# Revit family: 210_7b185d169fbb4492bceb13950c4227
name_source: partatom
category: Mechanical Equipment
units: mm (PartAtom-declared; Revit-internal decimal feet)

## family parameters
Always vertical = Yes
Cut with Voids When Loaded = No
Part Type = Breaks Into
Room Calculation Point = No
Round Connector Dimension = Use Diameter
Shared = No
Work Plane-Based = No

## types (1)
- ECo Flow 160S
    A2 = 155 mm  [stored 0.50853 ft]
    BB = 79 mm  [stored 0.259186 ft]
    BB_2 = 40 mm  [stored 0.131234 ft]
    BD = 36 mm  [stored 0.11811 ft]
    BP2 = 150 mm  [stored 0.492126 ft]
    CAT0 = Yes
    D = 160 mm
    Default Elevation = 0 mm  [stored 0 ft]
    Description = Roof fan
    H3 = 43 mm  [stored 0.141076 ft]
    H4 = 99 mm
    H5 = 20 mm  [stored 0.0656168 ft]
    H6 = 30 mm  [stored 0.0984252 ft]
    H7 = 246 mm
    HS = 8 mm  [stored 0.0262467 ft]
    HS__ve = -8 mm  [stored -0.0262467 ft]
    MC Product Code = ECo Flow 160S
    Manufacturer = Vilpe
    QmdConnectorList = 201;D
    R1 = 20 mm  [stored 0.0656168 ft]
    R2 = 105 mm
    R3 = 132 mm
    R31 = 143 mm
    R32 = 149 mm
    R4 = 151 mm  [stored 0.495407 ft]
    R5 = 147 mm
    R6 = 140 mm
    RS = 20 mm  [stored 0.0656168 ft]
    URL = vilpe.com
    W = 500 mm
    magiPartTypeId = 210
    magiProductFamilyId = 7b185d169fbb4492bceb13950c4227
    magiProductId = 0f5af643b2c943d1a88f0fb463d04b

note: [stored X ft] marks values corroborated as IEEE doubles in the binary element streams (Revit-internal decimal feet)
